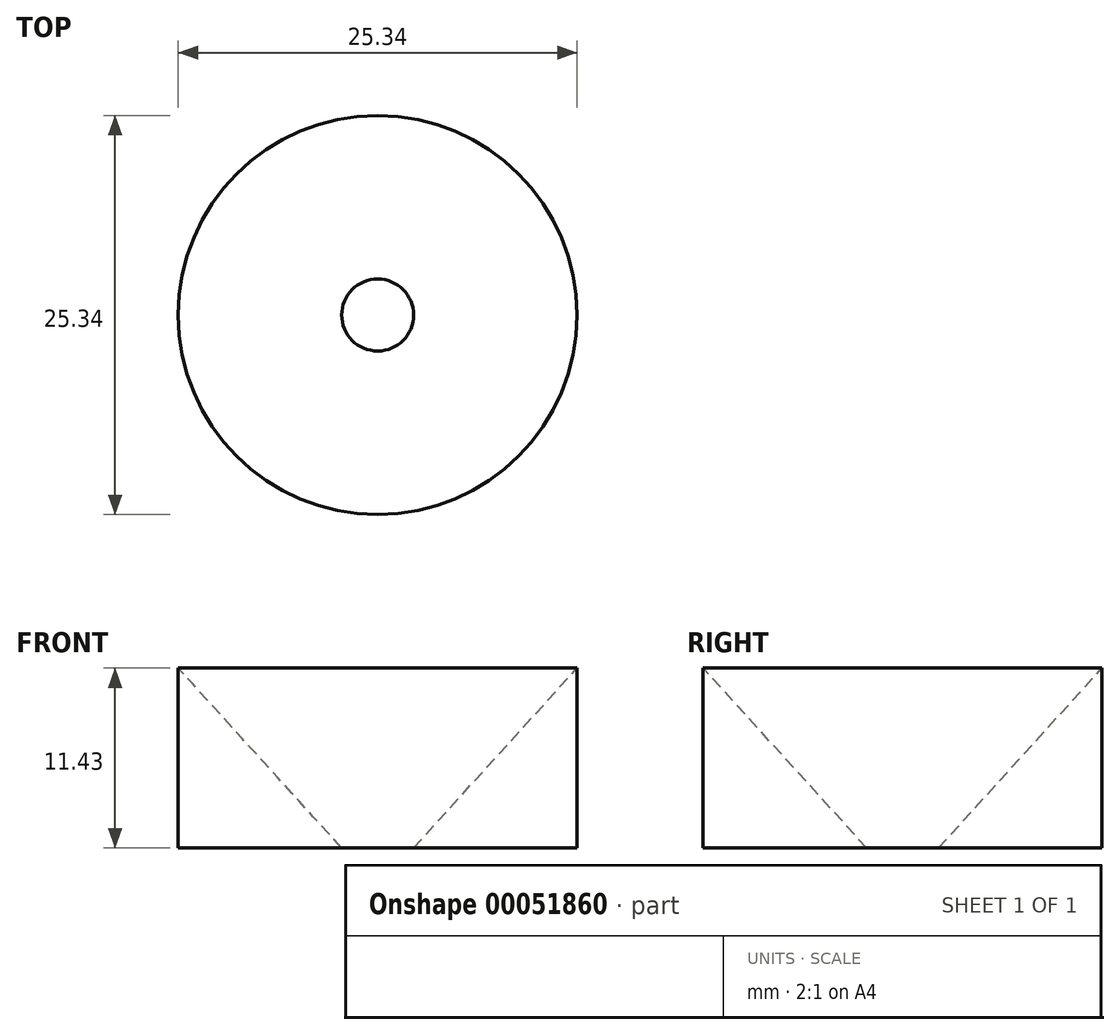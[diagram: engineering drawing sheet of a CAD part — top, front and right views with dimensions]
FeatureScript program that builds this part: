
annotation { "Feature Type Name" : "Feature", "Feature Type Description" : "" }
export const myFeature = defineFeature(function(context is Context, id is Id, definition is map)
    precondition{}
    {
        {
            var Q0;
            Q0=qCreatedBy(makeId("Front.planeOp"),FACE);
            var sketch = newSketch(context, id + "F0", { "sketchPlane" : qUnion([Q0])});
            skLineSegment(sketch, "E0", {"start": v(2.29, 0) * mm, "end": v(12.67, 11.43) * mm});
            skLineSegment(sketch, "E1", {"start": v(12.67, 11.43) * mm, "end": v(12.67, 0) * mm});
            skLineSegment(sketch, "E2", {"start": v(12.67, 0) * mm, "end": v(2.29, 0) * mm});
            skLineSegment(sketch, "E3", {"start": v(0, 0) * mm, "end": v(0, 14.1) * mm, "construction": true});
            skSolve(sketch);
        }
        {
            var Q0;
            Q0 = qSketchRegion(id + "F0", true);
            var Q1;
            Q1=sQuery(id+"F0.wireOp",EDGE,"E3");
            revolve(context, id + "F1", {"entities" : qUnion([Q0]), "axis" : qUnion([Q1]), "revolveType" : RevolveType.FULL});
        }
    });
